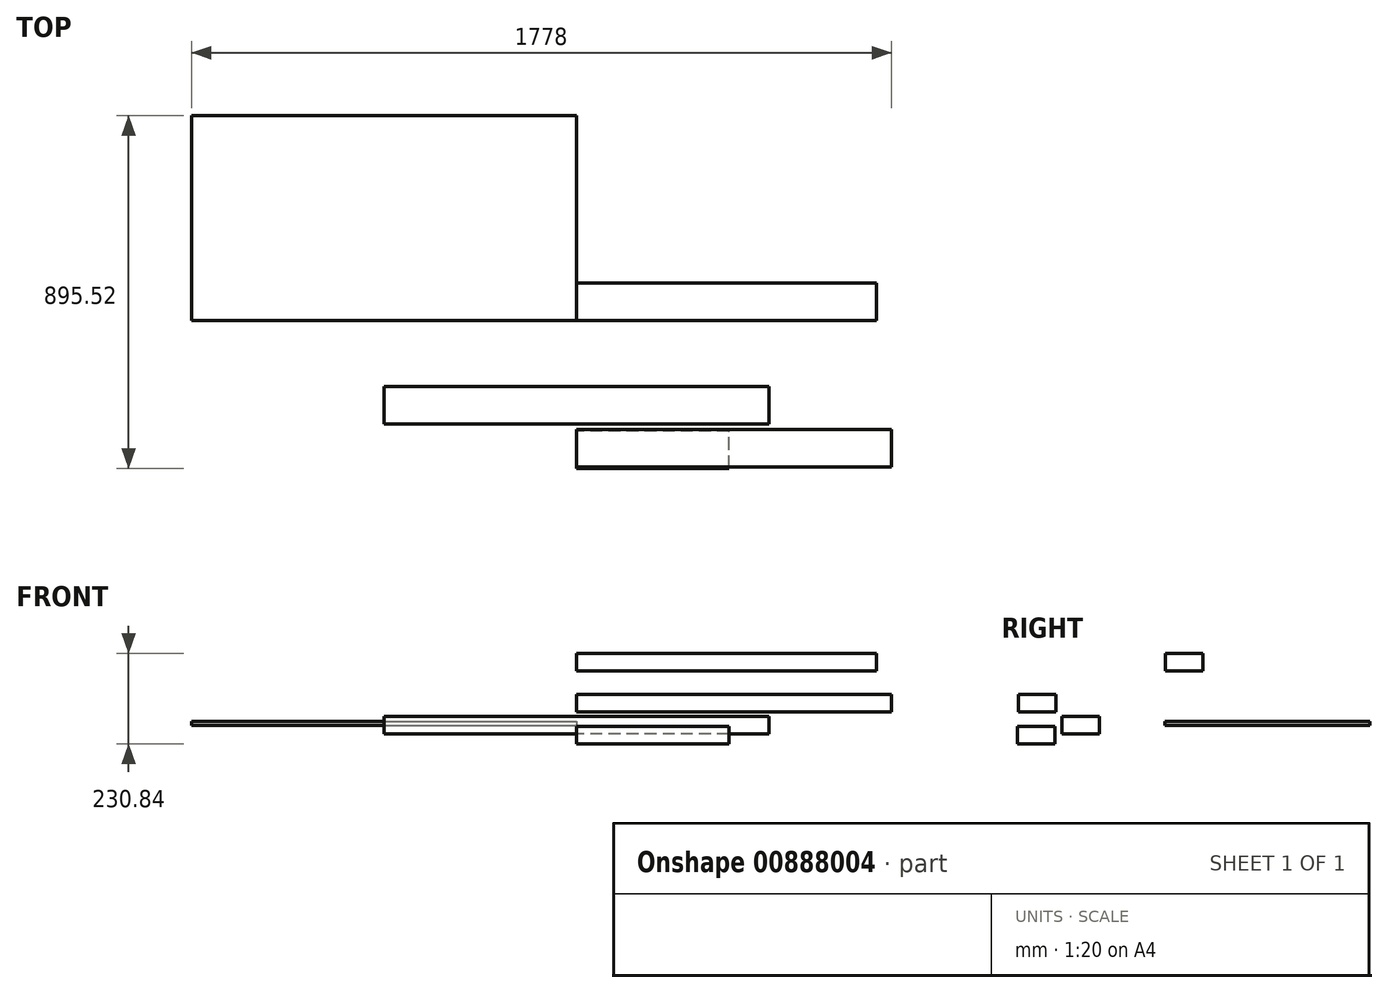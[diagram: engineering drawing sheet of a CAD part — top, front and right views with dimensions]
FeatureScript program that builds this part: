
annotation { "Feature Type Name" : "Feature", "Feature Type Description" : "" }
export const myFeature = defineFeature(function(context is Context, id is Id, definition is map)
    precondition{}
    {
        {
            var Q0;
            Q0=qCreatedBy(makeId("Right.planeOp"),FACE);
            var sketch = newSketch(context, id + "F0", { "sketchPlane" : qUnion([Q0])});
            skLineSegment(sketch, "E0.bottom", {"start": v(47.63, -22.22) * mm, "end": v(-47.63, -22.23) * mm});
            skLineSegment(sketch, "E0.top", {"start": v(47.63, 22.23) * mm, "end": v(-47.63, 22.22) * mm});
            skLineSegment(sketch, "E0.left", {"start": v(47.63, -22.22) * mm, "end": v(47.63, 22.23) * mm});
            skLineSegment(sketch, "E0.right", {"start": v(-47.63, -22.23) * mm, "end": v(-47.63, 22.22) * mm});
            skPoint(sketch, "E0.middle", {"position": v(0, 0) * mm});
            skSolve(sketch);
        }
        {
            var Q0;
            Q0=makeQuery(id+"F0.imprint","IMPRINT",FACE,{"disambiguationData":[TD([[makeQuery(id+"F0.imprint","IMPRINT",EDGE,{"derivedFrom":sQuery(id+"F0.wireOp",EDGE,"E0.bottom")}),-1.0]])]});
            extrude(context, id + "F1", {"entities" : qUnion([Q0]), "endBound" : BoundingType.SYMMETRIC, "depth" : 977.9 * mm, "offsetDistance" : 25.4 * mm});
        }
        {
            var Q0;
            Q0=qCreatedBy(makeId("Right.planeOp"),FACE);
            var sketch = newSketch(context, id + "F2", { "sketchPlane" : qUnion([Q0])});
            skLineSegment(sketch, "E1.bottom", {"start": v(215.37, 138.52) * mm, "end": v(310.62, 138.52) * mm});
            skLineSegment(sketch, "E1.top", {"start": v(215.37, 182.97) * mm, "end": v(310.62, 182.97) * mm});
            skLineSegment(sketch, "E1.left", {"start": v(215.37, 138.52) * mm, "end": v(215.37, 182.97) * mm});
            skLineSegment(sketch, "E1.right", {"start": v(310.62, 138.52) * mm, "end": v(310.62, 182.97) * mm});
            skSolve(sketch);
        }
        {
            var Q0;
            Q0=makeQuery(id+"F2.imprint","IMPRINT",FACE,{"disambiguationData":[TD([[makeQuery(id+"F2.imprint","IMPRINT",EDGE,{"derivedFrom":sQuery(id+"F2.wireOp",EDGE,"E1.bottom")}),1.0]])]});
            extrude(context, id + "F3", {"entities" : qUnion([Q0]), "depth" : 762 * mm, "offsetDistance" : 25.4 * mm});
        }
        {
            var Q0;
            Q0=qCreatedBy(makeId("Right.planeOp"),FACE);
            var sketch = newSketch(context, id + "F4", { "sketchPlane" : qUnion([Q0])});
            skLineSegment(sketch, "E2.bottom", {"start": v(-157.4, 77.76) * mm, "end": v(-62.15, 77.76) * mm});
            skLineSegment(sketch, "E2.top", {"start": v(-157.4, 33.31) * mm, "end": v(-62.15, 33.31) * mm});
            skLineSegment(sketch, "E2.left", {"start": v(-157.4, 77.76) * mm, "end": v(-157.4, 33.31) * mm});
            skLineSegment(sketch, "E2.right", {"start": v(-62.15, 77.76) * mm, "end": v(-62.15, 33.31) * mm});
            skSolve(sketch);
        }
        {
            var Q0;
            Q0=qSketchRegion(id+"F4",true);
            extrude(context, id + "F5", {"entities" : qUnion([Q0]), "depth" : 800.1 * mm, "offsetDistance" : 25.4 * mm});
        }
        {
            var Q0;
            Q0=qCreatedBy(makeId("Right.planeOp"),FACE);
            var sketch = newSketch(context, id + "F6", { "sketchPlane" : qUnion([Q0])});
            skLineSegment(sketch, "E3.bottom", {"start": v(-160.34, -3.42) * mm, "end": v(-65.1, -3.42) * mm});
            skLineSegment(sketch, "E3.top", {"start": v(-160.34, -47.87) * mm, "end": v(-65.1, -47.87) * mm});
            skLineSegment(sketch, "E3.left", {"start": v(-160.34, -3.42) * mm, "end": v(-160.34, -47.87) * mm});
            skLineSegment(sketch, "E3.right", {"start": v(-65.1, -3.42) * mm, "end": v(-65.1, -47.87) * mm});
            skSolve(sketch);
        }
        {
            var Q0;
            Q0=qSketchRegion(id+"F6",true);
            extrude(context, id + "F7", {"entities" : qUnion([Q0]), "depth" : 387.35 * mm, "offsetDistance" : 25.4 * mm});
        }
        {
            var Q0;
            Q0=qCreatedBy(makeId("Top.planeOp"),FACE);
            var sketch = newSketch(context, id + "F8", { "sketchPlane" : qUnion([Q0])});
            skLineSegment(sketch, "E4.bottom", {"start": v(-977.9, 735.18) * mm, "end": v(0, 735.18) * mm});
            skLineSegment(sketch, "E4.top", {"start": v(-977.9, 214.48) * mm, "end": v(0, 214.48) * mm});
            skLineSegment(sketch, "E4.left", {"start": v(-977.9, 735.18) * mm, "end": v(-977.9, 214.48) * mm});
            skLineSegment(sketch, "E4.right", {"start": v(0, 735.18) * mm, "end": v(0, 214.48) * mm});
            skSolve(sketch);
        }
        {
            var Q0;
            Q0=qSketchRegion(id+"F8",true);
            extrude(context, id + "F9", {"entities" : qUnion([Q0]), "depth" : 9.52 * mm, "offsetDistance" : 25.4 * mm});
        }
    });
